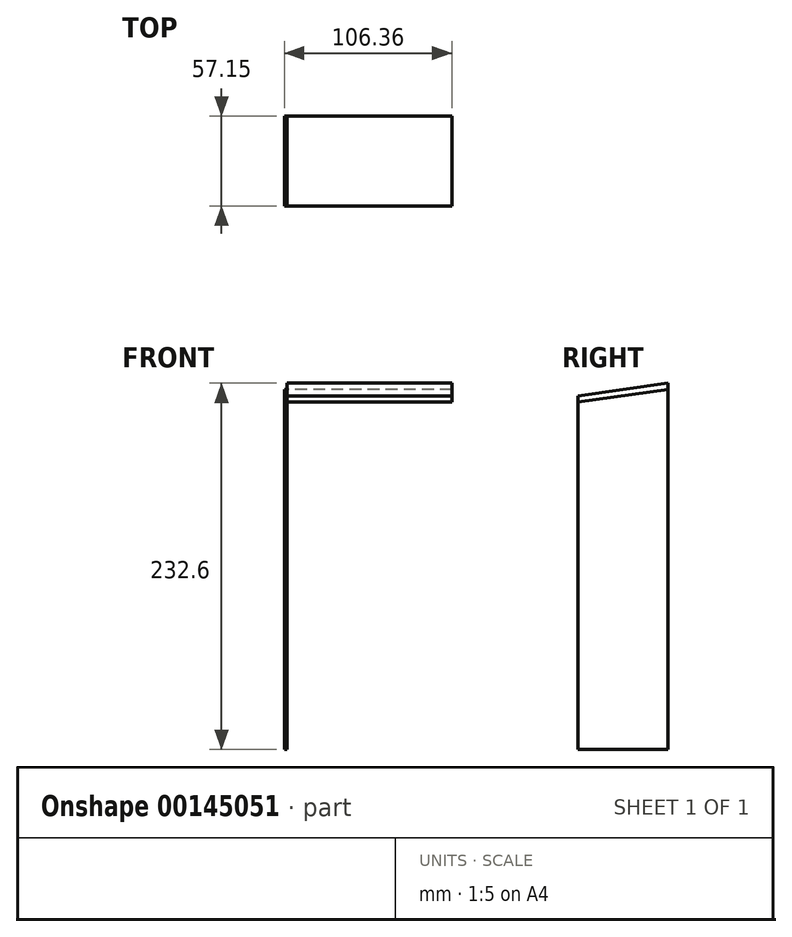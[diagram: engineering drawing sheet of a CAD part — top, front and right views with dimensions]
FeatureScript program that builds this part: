
annotation { "Feature Type Name" : "Feature", "Feature Type Description" : "" }
export const myFeature = defineFeature(function(context is Context, id is Id, definition is map)
    precondition{}
    {
        {
            var Q0;
            Q0=qCreatedBy(makeId("Front.planeOp"),FACE);
            var sketch = newSketch(context, id + "F0", { "sketchPlane" : qUnion([Q0])});
            skLineSegment(sketch, "E0.bottom", {"start": v(-43.5, 181.24) * mm, "end": v(-41.91, 181.24) * mm});
            skLineSegment(sketch, "E0.top", {"start": v(-43.5, -47.36) * mm, "end": v(-41.91, -47.36) * mm});
            skLineSegment(sketch, "E0.left", {"start": v(-43.5, 181.24) * mm, "end": v(-43.5, -47.36) * mm});
            skLineSegment(sketch, "E0.right", {"start": v(-41.91, 181.24) * mm, "end": v(-41.91, -47.36) * mm});
            skSolve(sketch);
        }
        {
            var Q0;
            Q0 = qSketchRegion(id + "F0", true);
            extrude(context, id + "F1", {"entities" : qUnion([Q0]), "depth" : 57.15 * mm});
        }
        {
            var Q0;
            Q0=makeQuery(id+"F1.opExtrude","SWEPT_FACE",FACE,{"disambiguationData":[OSD([sQuery(id+"F0.wireOp",EDGE,"E0.left")])]});
            var sketch = newSketch(context, id + "F2", { "sketchPlane" : qUnion([Q0])});
            skLineSegment(sketch, "E1", {"start": v(0, 181.24) * mm, "end": v(57.15, 173.21) * mm});
            skLineSegment(sketch, "E2", {"start": v(57.15, 173.21) * mm, "end": v(57.15, 181.24) * mm});
            skLineSegment(sketch, "E3", {"start": v(57.15, 181.24) * mm, "end": v(0, 181.24) * mm});
            skSolve(sketch);
        }
        {
            var Q0;
            Q0 = qSketchRegion(id + "F2", true);
            extrude(context, id + "F3", {"entities" : qUnion([Q0]), "operationType" : NewBodyOperationType.REMOVE, "endBound" : BoundingType.UP_TO_NEXT, "oppositeDirection" : true, "depth" : 25.4 * mm});
        }
        {
            var Q0;
            Q0=makeQuery(id+"F1.opExtrude","SWEPT_FACE",FACE,{"disambiguationData":[OSD([sQuery(id+"F0.wireOp",EDGE,"E0.right")])]});
            var sketch = newSketch(context, id + "F4", { "sketchPlane" : qUnion([Q0])});
            skLineSegment(sketch, "E4", {"start": v(-57.15, 173.21) * mm, "end": v(0, 181.24) * mm});
            skLineSegment(sketch, "E5", {"start": v(0, 185.24) * mm, "end": v(0, 181.24) * mm});
            skLineSegment(sketch, "E6", {"start": v(0, 185.24) * mm, "end": v(-57.15, 177.14) * mm});
            skLineSegment(sketch, "E7", {"start": v(-57.15, 173.21) * mm, "end": v(-57.15, 177.14) * mm});
            skSolve(sketch);
        }
        {
            var Q0;
            Q0 = qSketchRegion(id + "F4", true);
            extrude(context, id + "F5", {"entities" : qUnion([Q0]), "depth" : 104.77 * mm});
        }
    });
